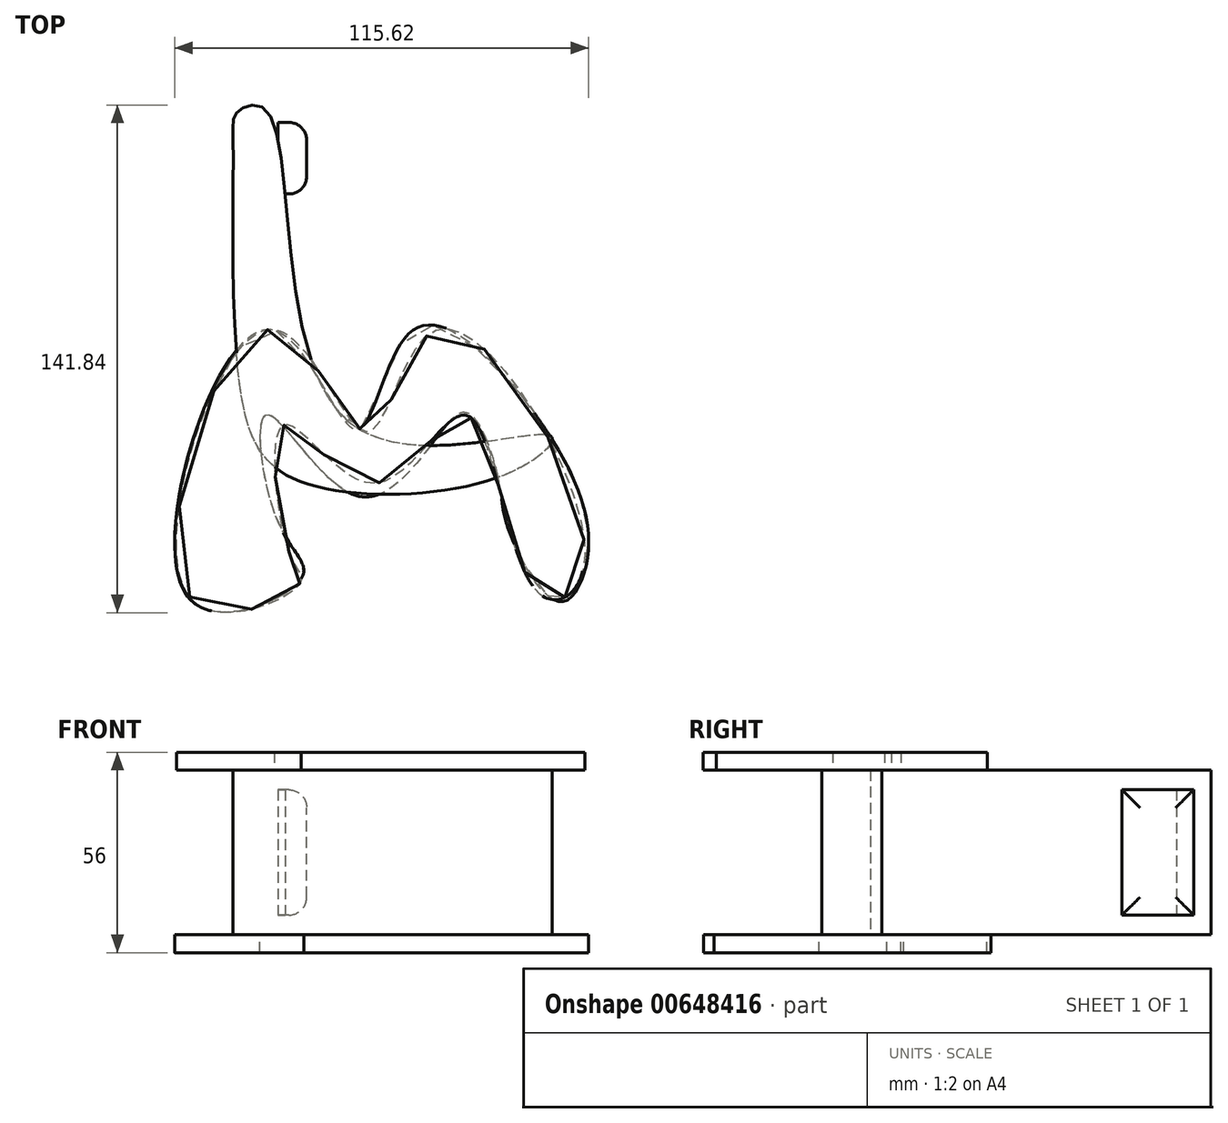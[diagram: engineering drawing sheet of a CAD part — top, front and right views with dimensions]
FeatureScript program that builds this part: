
annotation { "Feature Type Name" : "Feature", "Feature Type Description" : "" }
export const myFeature = defineFeature(function(context is Context, id is Id, definition is map)
    precondition{}
    {
        {
            var Q0;
            Q0=qCreatedBy(makeId("Top.planeOp"),FACE);
            var sketch = newSketch(context, id + "F0", { "sketchPlane" : qUnion([Q0])});
            skFitSpline(sketch, "E0", {"points": [v(-40.87, 60.66) * mm, v(-18.1, -25.94) * mm, v(37.9, -29.68) * mm, v(27.45, -39.76) * mm, v(-31.16, -42.74) * mm, v(-48.33, -18.1) * mm, v(-50.57, 52.82) * mm, v(-49.08, 61.04) * mm, v(-40.87, 60.66) * mm]});
            skSolve(sketch);
        }
        {
            var Q0;
            Q0=makeQuery(id+"F0.imprint","IMPRINT",FACE,{"disambiguationData":[TD([[makeQuery(id+"F0.imprint","IMPRINT",EDGE,{"derivedFrom":sQuery(id+"F0.wireOp",EDGE,"E0")}),-1.0]])]});
            extrude(context, id + "F1", {"entities" : qUnion([Q0]), "endBound" : BoundingType.SYMMETRIC, "depth" : 46 * mm, "offsetDistance" : 25 * mm});
        }
        {
            var Q0;
            Q0=qCreatedBy(makeId("Top.planeOp"),FACE);
            cPlane(context, id + "F2", {"entities" : qUnion([Q0]), "cplaneType" : CPlaneType.OFFSET, "offset" : 23 * mm, "width" : 150 * mm, "height" : 150 * mm});
        }
        {
            var Q0;
            Q0=qCreatedBy(makeId("Top.planeOp"),FACE);
            cPlane(context, id + "F3", {"entities" : qUnion([Q0]), "cplaneType" : CPlaneType.OFFSET, "offset" : 23 * mm, "oppositeDirection" : true, "width" : 150 * mm, "height" : 150 * mm});
        }
        {
            var Q0;
            Q0=qCreatedBy(id+"F2.planeOp",FACE);
            var sketch = newSketch(context, id + "F4", { "sketchPlane" : qUnion([Q0])});
            skFitSpline(sketch, "E1", {"points": [v(-62.74, -74.84) * mm, v(-40.2, 0) * mm, v(-13.16, -28.58) * mm, v(6.76, 0) * mm, v(47.56, -64.64) * mm, v(34.75, -73.65) * mm, v(14.59, -24.08) * mm, v(-11.03, -43.05) * mm, v(-36.17, -26.68) * mm, v(-34.75, -62.74) * mm, v(-32.38, -71.75) * mm, v(-62.74, -74.84) * mm]});
            skSolve(sketch);
        }
        {
            var Q0;
            Q0=makeQuery(id+"F4.imprint","IMPRINT",FACE,{"disambiguationData":[TD([[makeQuery(id+"F4.imprint","IMPRINT",EDGE,{"derivedFrom":sQuery(id+"F4.wireOp",EDGE,"E1")}),-1.0]])]});
            extrude(context, id + "F5", {"entities" : qUnion([Q0]), "operationType" : NewBodyOperationType.ADD, "depth" : 5 * mm, "offsetDistance" : 25 * mm});
        }
        {
            var Q0;
            Q0=qCreatedBy(id+"F3.planeOp",FACE);
            var sketch = newSketch(context, id + "F6", { "sketchPlane" : qUnion([Q0])});
            skFitSpline(sketch, "E2", {"points": [v(-63.26, -74.69) * mm, v(-40.97, 0) * mm, v(-16.3, -27.96) * mm, v(0, 0) * mm, v(38.26, -30.33) * mm, v(48.22, -64.96) * mm, v(40.4, -76.1) * mm, v(26.16, -55.47) * mm, v(23.55, -41.71) * mm, v(15.01, -23.45) * mm, v(4.58, -32.46) * mm, v(-17.01, -46.22) * mm, v(-41.2, -23.92) * mm, v(-37.4, -55.23) * mm, v(-31.72, -69.94) * mm, v(-63.26, -74.69) * mm]});
            skSolve(sketch);
        }
        {
            var Q0;
            Q0 = qSketchRegion(id + "F6", true);
            extrude(context, id + "F7", {"entities" : qUnion([Q0]), "operationType" : NewBodyOperationType.ADD, "oppositeDirection" : true, "depth" : 5 * mm, "offsetDistance" : 25 * mm});
        }
        {
            var Q0;
            Q0=qCreatedBy(makeId("Right.planeOp"),FACE);
            cPlane(context, id + "F8", {"entities" : qUnion([Q0]), "cplaneType" : CPlaneType.OFFSET, "offset" : 38 * mm, "oppositeDirection" : true, "width" : 150 * mm, "height" : 150 * mm});
        }
        {
            var Q0;
            Q0=qCreatedBy(id+"F8.planeOp",FACE);
            var sketch = newSketch(context, id + "F9", { "sketchPlane" : qUnion([Q0])});
            skLineSegment(sketch, "E3.bottom", {"start": v(37.8, -17.5) * mm, "end": v(57.8, -17.5) * mm});
            skLineSegment(sketch, "E3.top", {"start": v(37.8, 17.5) * mm, "end": v(57.8, 17.5) * mm});
            skLineSegment(sketch, "E3.left", {"start": v(37.8, -17.5) * mm, "end": v(37.8, 17.5) * mm});
            skLineSegment(sketch, "E3.right", {"start": v(57.8, -17.5) * mm, "end": v(57.8, 17.5) * mm});
            skPoint(sketch, "E3.middle", {"position": v(47.8, 0) * mm});
            skSolve(sketch);
        }
        {
            var Q0;
            Q0 = qSketchRegion(id + "F9", true);
            extrude(context, id + "F10", {"entities" : qUnion([Q0]), "operationType" : NewBodyOperationType.ADD, "depth" : 8 * mm, "offsetDistance" : 25 * mm});
        }
        {
            var Q0;
            Q0=makeQuery(id+"F10.opExtrude","CAP_FACE",FACE,{"disambiguationData":[OSD([sQuery(id+"F9.wireOp",EDGE,"E3.bottom"),sQuery(id+"F9.wireOp",EDGE,"E3.top"),sQuery(id+"F9.wireOp",EDGE,"E3.left"),sQuery(id+"F9.wireOp",EDGE,"E3.right")])],"isStart":false});
            fillet(context, id + "F11", {"entities" : qUnion([Q0]), "radius" : 5 * mm, "tangentPropagation" : true, "allowEdgeOverflow" : false});
        }
    });
